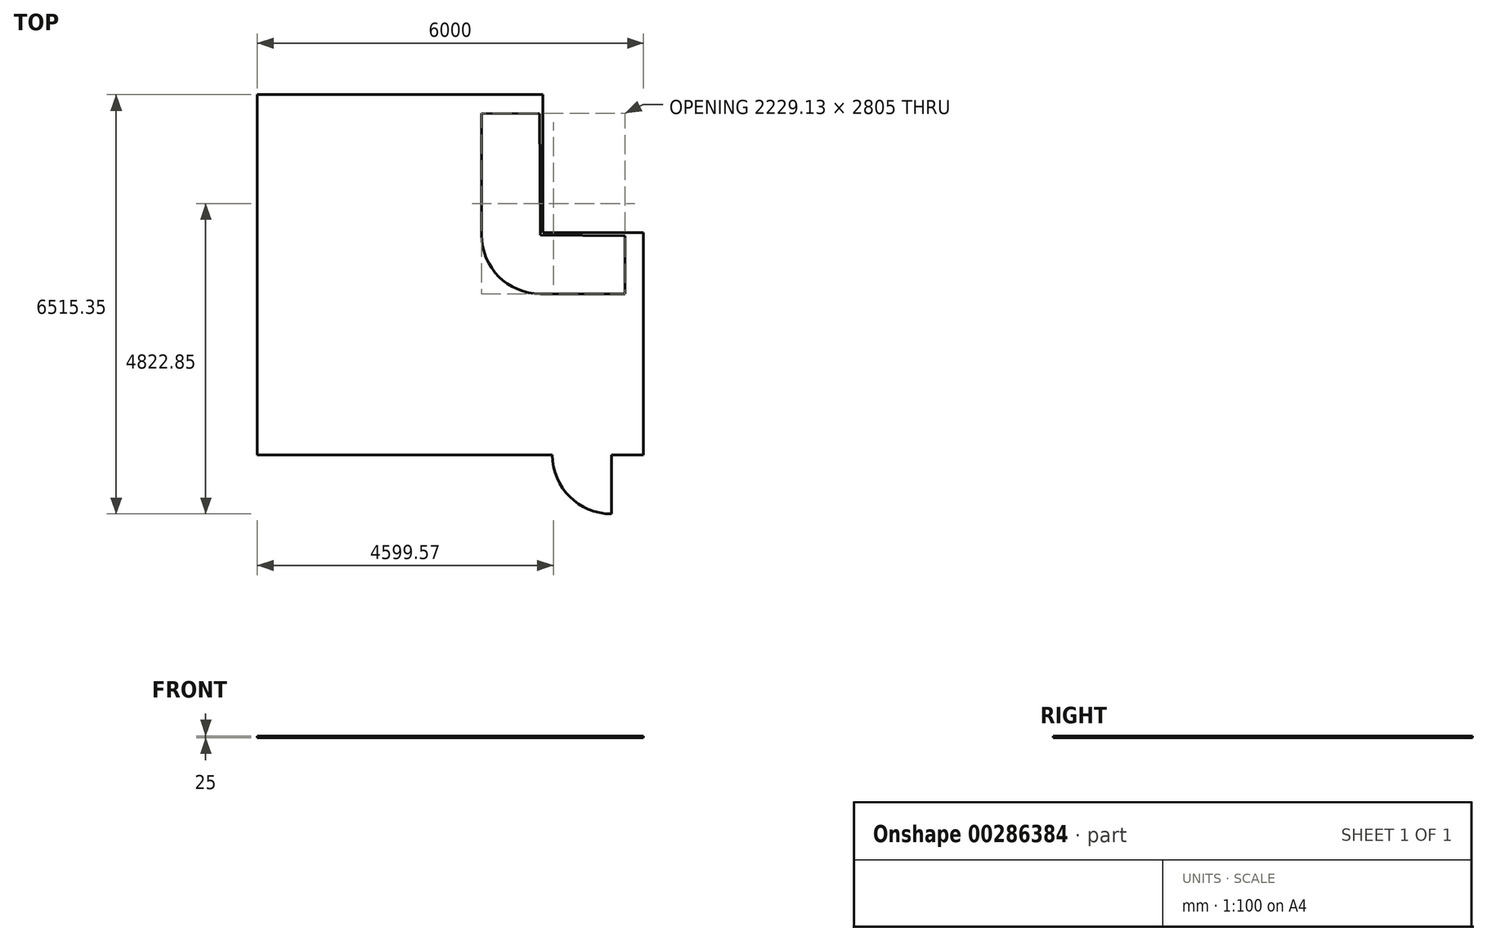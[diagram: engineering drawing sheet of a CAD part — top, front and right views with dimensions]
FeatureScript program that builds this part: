
annotation { "Feature Type Name" : "Feature", "Feature Type Description" : "" }
export const myFeature = defineFeature(function(context is Context, id is Id, definition is map)
    precondition{}
    {
        {
            var Q0;
            Q0=qCreatedBy(makeId("Top.planeOp"),FACE);
            var sketch = newSketch(context, id + "F0", { "sketchPlane" : qUnion([Q0])});
            skLineSegment(sketch, "E0", {"start": v(0, 0) * mm, "end": v(0, -5600) * mm});
            skLineSegment(sketch, "E1", {"start": v(0, 0) * mm, "end": v(3485, 0) * mm});
            skLineSegment(sketch, "E2", {"start": v(0, -5600) * mm, "end": v(4590, -5600) * mm});
            skLineSegment(sketch, "E3", {"start": v(5500, -5600) * mm, "end": v(6000, -5600) * mm});
            skLineSegment(sketch, "E4", {"start": v(6000, -5600) * mm, "end": v(6000, -3095) * mm});
            skLineSegment(sketch, "E5", {"start": v(3485, 0) * mm, "end": v(3485, -2185) * mm});
            skLineSegment(sketch, "E6", {"start": v(4395, -3095) * mm, "end": v(6000, -3095) * mm});
            skPoint(sketch, "E7.visualSharp", {"position": v(3485, -3095) * mm});
            skArc(sketch, "E7.filletArc", {"start": v(3485, -2185) * mm, "mid": v(3751.53, -2828.47) * mm, "end": v(4395, -3095) * mm});
            skArc(sketch, "E8", {"start": v(4584.65, -5600) * mm, "mid": v(4852.75, -6247.25) * mm, "end": v(5500, -6515.35) * mm});
            skLineSegment(sketch, "E9", {"start": v(5500, -5600) * mm, "end": v(5500, -6515.35) * mm});
            skLineSegment(sketch, "E10", {"start": v(3485, 0) * mm, "end": v(4385, 0) * mm});
            skLineSegment(sketch, "E11", {"start": v(4385, 0) * mm, "end": v(4395, -2185) * mm});
            skLineSegment(sketch, "E12", {"start": v(6000, -3095) * mm, "end": v(6000, -2195) * mm});
            skLineSegment(sketch, "E13", {"start": v(6000, -2195) * mm, "end": v(4395, -2185) * mm});
            skLineSegment(sketch, "E14", {"start": v(3485, 0) * mm, "end": v(3485, -290) * mm});
            skLineSegment(sketch, "E15", {"start": v(3485, -290) * mm, "end": v(3485, -580) * mm});
            skLineSegment(sketch, "E16", {"start": v(3485, -580) * mm, "end": v(3485, -870) * mm});
            skLineSegment(sketch, "E17", {"start": v(3485, -870) * mm, "end": v(3485, -1092.5) * mm});
            skLineSegment(sketch, "E18", {"start": v(3485, -1092.5) * mm, "end": v(3485, -1382.5) * mm});
            skLineSegment(sketch, "E19", {"start": v(3485, -1382.5) * mm, "end": v(3485, -1672.5) * mm});
            skLineSegment(sketch, "E20", {"start": v(3485, -1672.5) * mm, "end": v(3485, -1962.5) * mm});
            skLineSegment(sketch, "E21", {"start": v(3485, -290) * mm, "end": v(4395, -295.67) * mm});
            skLineSegment(sketch, "E22", {"start": v(3485, -580) * mm, "end": v(4387.68, -585.62) * mm});
            skLineSegment(sketch, "E23", {"start": v(3485, -870) * mm, "end": v(4395, -865.84) * mm});
            skLineSegment(sketch, "E24", {"start": v(3485, -1092.5) * mm, "end": v(4395, -1098.17) * mm});
            skLineSegment(sketch, "E25", {"start": v(3485, -1382.5) * mm, "end": v(4395, -1388.17) * mm});
            skLineSegment(sketch, "E26", {"start": v(3485, -1672.5) * mm, "end": v(4395, -1678.17) * mm});
            skLineSegment(sketch, "E27", {"start": v(3485, -1962.5) * mm, "end": v(4395, -1968.17) * mm});
            skLineSegment(sketch, "E28", {"start": v(6000, -2195) * mm, "end": v(5710, -2193.2) * mm});
            skLineSegment(sketch, "E29", {"start": v(5710, -2193.2) * mm, "end": v(5420.01, -2191.39) * mm});
            skLineSegment(sketch, "E30", {"start": v(5420.01, -2191.39) * mm, "end": v(5130.02, -2189.58) * mm});
            skLineSegment(sketch, "E31", {"start": v(5130.02, -2189.58) * mm, "end": v(4840.02, -2187.77) * mm});
            skLineSegment(sketch, "E32", {"start": v(4840.02, -2187.77) * mm, "end": v(4840.02, -3095) * mm});
            skLineSegment(sketch, "E33", {"start": v(5130.02, -2189.58) * mm, "end": v(5134.16, -3095) * mm});
            skLineSegment(sketch, "E34", {"start": v(5420.01, -2191.39) * mm, "end": v(5424.15, -3095) * mm});
            skLineSegment(sketch, "E35", {"start": v(5710, -2193.2) * mm, "end": v(5714.13, -3095) * mm});
            skLineSegment(sketch, "E36", {"start": v(4385, 0) * mm, "end": v(4435, -0.31) * mm});
            skLineSegment(sketch, "E37", {"start": v(4435, -0.31) * mm, "end": v(4435, -2185.25) * mm});
            skLineSegment(sketch, "E38", {"start": v(6000, -2195) * mm, "end": v(5999.77, -2145) * mm});
            skLineSegment(sketch, "E39", {"start": v(5999.77, -2145) * mm, "end": v(4435, -2145) * mm});
            skSolve(sketch);
        }
        {
            var Q0;
            Q0 = qSketchRegion(id + "F0", true);
            extrude(context, id + "F1", {"entities" : qUnion([Q0]), "depth" : 25 * mm});
        }
    });
